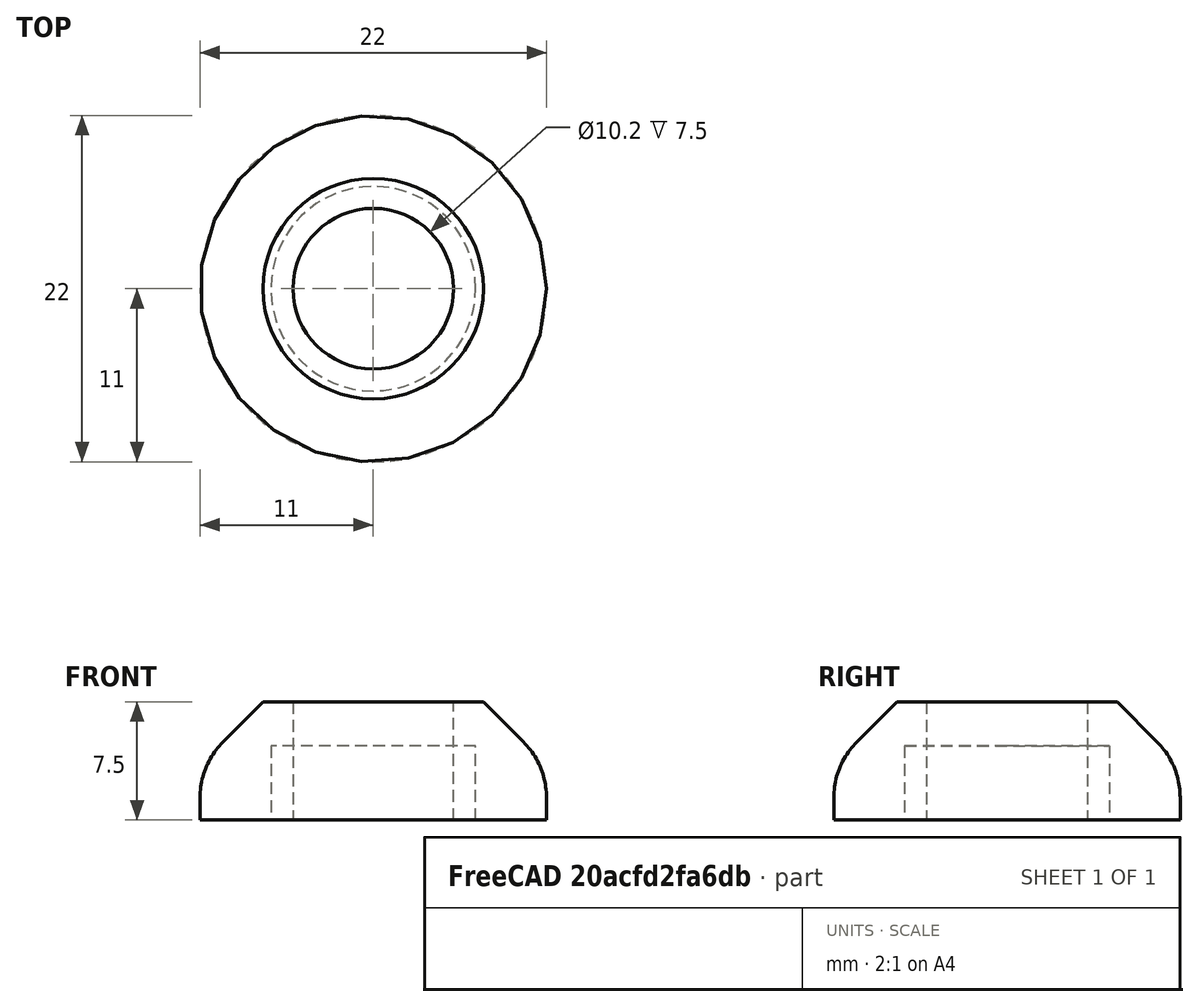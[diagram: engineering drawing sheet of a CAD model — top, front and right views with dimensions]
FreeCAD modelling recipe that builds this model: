
FCSTD DOCUMENT  (FreeCAD 0.16R)
Label: 10mm spacer thing
License: All rights reserved
LicenseURL: http://en.wikipedia.org/wiki/All_rights_reserved
objects: Sketcher::SketchObject×2, PartDesign::Pad×1, PartDesign::Chamfer×1, PartDesign::Fillet×1, PartDesign::Pocket×1, Mesh::Feature×1
note: 8 computed .brp shape members not serialized (recipe doc carries the construction recipe); baked Part::Feature solids carry a one-line shape summary decoded from their .brp

FEATURE [Sketcher::SketchObject] Sketch
  sketch-geometry (2):
    g0: Circle CenterX=0 CenterY=0 CenterZ=0 NormalX=0 NormalY=0 NormalZ=1 Radius=5.1
    g1: Circle CenterX=0 CenterY=0 CenterZ=0 NormalX=0 NormalY=0 NormalZ=1 Radius=11
  constraints (4):
    c: Coincident(g0,g-1)
    c: Coincident(g1,g-1)
    c: Radius(g1) = 11
    c: Radius(g0) = 5.1
FEATURE [PartDesign::Pad] Pad
  Length = 7.5
  Length2 = 100
  Sketch = -> Sketch
  Type = 0
FEATURE [PartDesign::Chamfer] Chamfer
  Base = -> Pad [Edge3]
  Size = 4
FEATURE [PartDesign::Fillet] Fillet
  Base = -> Chamfer [Edge2]
  Radius = 5
FEATURE [Sketcher::SketchObject] Sketch001
  Placement = pos=(0,0,0) rot=(1,0,0;3.14159rad)
  Support = -> Fillet [Face3]
  sketch-geometry (1):
    g0: Circle CenterX=0 CenterY=0 CenterZ=0 NormalX=0 NormalY=0 NormalZ=1 Radius=6.5
  constraints (2):
    c: Coincident(g0,g-1)
    c: Radius(g0) = 6.5
FEATURE [PartDesign::Pocket] Pocket
  Length = 4.7
  Sketch = -> Sketch001
  Type = 0
FEATURE [Mesh::Feature] Mesh  label="Pocket (Meshed)"
